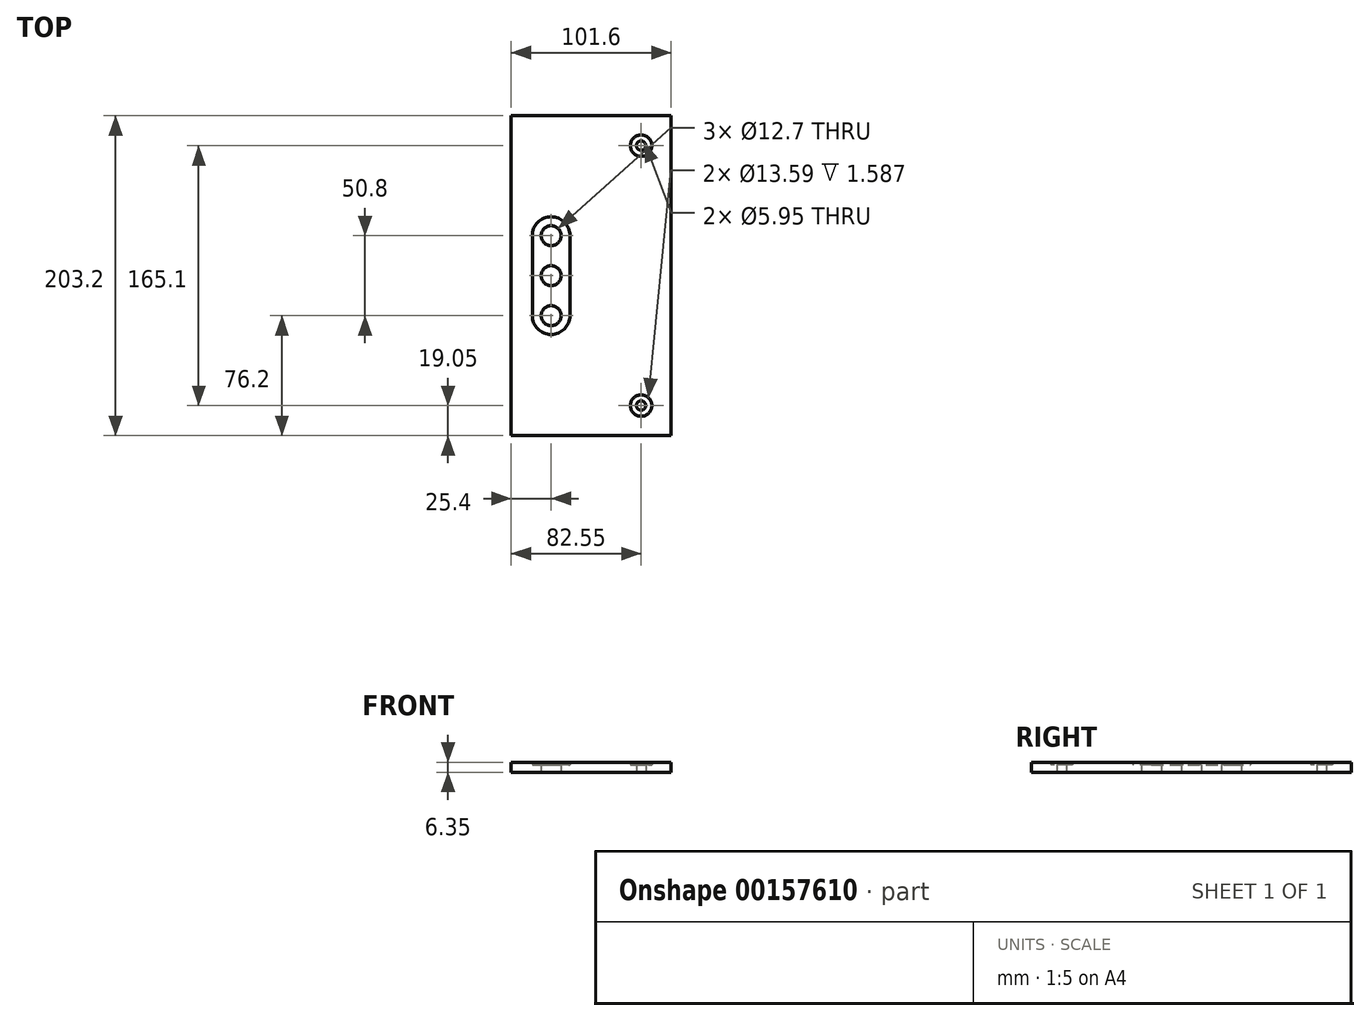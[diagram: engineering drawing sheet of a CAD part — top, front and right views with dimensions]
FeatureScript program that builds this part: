
annotation { "Feature Type Name" : "Feature", "Feature Type Description" : "" }
export const myFeature = defineFeature(function(context is Context, id is Id, definition is map)
    precondition{}
    {
        {
            var Q0;
            Q0=qCreatedBy(makeId("Top.planeOp"),FACE);
            var sketch = newSketch(context, id + "F0", { "sketchPlane" : qUnion([Q0])});
            skLineSegment(sketch, "E0.bottom", {"start": v(0, 0) * mm, "end": v(203.2, 0) * mm});
            skLineSegment(sketch, "E0.top", {"start": v(0, 101.6) * mm, "end": v(203.2, 101.6) * mm});
            skLineSegment(sketch, "E0.left", {"start": v(0, 0) * mm, "end": v(0, 101.6) * mm});
            skLineSegment(sketch, "E0.right", {"start": v(203.2, 0) * mm, "end": v(203.2, 101.6) * mm});
            skCircle(sketch, "E1", {"center": v(76.2, 76.2) * mm, "radius": 6.35 * mm});
            skCircle(sketch, "E2", {"center": v(101.6, 76.2) * mm, "radius": 6.35 * mm});
            skCircle(sketch, "E3", {"center": v(127, 76.2) * mm, "radius": 6.35 * mm});
            skArc(sketch, "E4", {"start": v(76.2, 88.17) * mm, "mid": v(64.23, 76.2) * mm, "end": v(76.2, 64.23) * mm});
            skArc(sketch, "E5", {"start": v(127, 64.23) * mm, "mid": v(138.97, 76.2) * mm, "end": v(127, 88.17) * mm});
            skLineSegment(sketch, "E6", {"start": v(76.2, 88.17) * mm, "end": v(127, 88.17) * mm});
            skLineSegment(sketch, "E7", {"start": v(76.2, 64.23) * mm, "end": v(127, 64.23) * mm});
            skCircle(sketch, "E8", {"center": v(19.05, 19.05) * mm, "radius": 6.8 * mm});
            skCircle(sketch, "E9", {"center": v(19.05, 19.05) * mm, "radius": 2.98 * mm});
            skCircle(sketch, "E10", {"center": v(184.15, 19.05) * mm, "radius": 6.8 * mm});
            skCircle(sketch, "E11", {"center": v(184.15, 19.05) * mm, "radius": 2.98 * mm});
            skSolve(sketch);
        }
        {
            var Q0;
            Q0=makeQuery(id+"F0.imprint","IMPRINT",FACE,{"disambiguationData":[TD([[makeQuery(id+"F0.imprint","IMPRINT",EDGE,{"derivedFrom":sQuery(id+"F0.wireOp",EDGE,"E1")}),-1.0]])]});
            extrude(context, id + "F1", {"entities" : qUnion([Q0]), "depth" : 4.76 * mm});
        }
        {
            var Q0;
            Q0=makeQuery(id+"F0.imprint","IMPRINT",FACE,{"disambiguationData":[TD([[makeQuery(id+"F0.imprint","IMPRINT",EDGE,{"derivedFrom":sQuery(id+"F0.wireOp",EDGE,"E0.bottom")}),1.0]])]});
            extrude(context, id + "F2", {"entities" : qUnion([Q0]), "operationType" : NewBodyOperationType.ADD, "depth" : 6.35 * mm});
        }
        {
            var Q0;
            Q0=makeQuery(id+"F0.imprint","IMPRINT",FACE,{"disambiguationData":[TD([[makeQuery(id+"F0.imprint","IMPRINT",EDGE,{"derivedFrom":sQuery(id+"F0.wireOp",EDGE,"E8")}),1.0]])]});
            extrude(context, id + "F3", {"entities" : qUnion([Q0]), "operationType" : NewBodyOperationType.ADD, "depth" : 4.76 * mm});
        }
        {
            var Q0;
            Q0=makeQuery(id+"F0.imprint","IMPRINT",FACE,{"disambiguationData":[TD([[makeQuery(id+"F0.imprint","IMPRINT",EDGE,{"derivedFrom":sQuery(id+"F0.wireOp",EDGE,"E10")}),1.0]])]});
            extrude(context, id + "F4", {"entities" : qUnion([Q0]), "operationType" : NewBodyOperationType.ADD, "depth" : 4.76 * mm});
        }
        {
            var Q0;
            Q0=makeQuery(id+"F1.opExtrude","SWEPT_BODY",BODY,{"disambiguationData":[OSD([sQuery(id+"F0.wireOp",EDGE,"E1"),sQuery(id+"F0.wireOp",EDGE,"E2"),sQuery(id+"F0.wireOp",EDGE,"E3"),sQuery(id+"F0.wireOp",EDGE,"E4"),sQuery(id+"F0.wireOp",EDGE,"E5"),sQuery(id+"F0.wireOp",EDGE,"E6"),sQuery(id+"F0.wireOp",EDGE,"E7")])]});
            var Q1;
            Q1=makeQuery(id+"F2.opExtrude","SWEPT_EDGE",EDGE,{"disambiguationData":[OSD([sQuery(id+"F0.wireOp",EDGE,"E0.bottom"),sQuery(id+"F0.wireOp",EDGE,"E0.left")])]});
            transform(context, id + "F5", {"entities" : qUnion([Q0]), "transformType" : TransformType.ROTATION, "transformAxis" : qUnion([Q1]), "angle" : 270 * degree, "makeCopy" : false});
        }
        {
            var Q0;
            Q0=makeQuery(id+"F1.opExtrude","SWEPT_BODY",BODY,{"disambiguationData":[OSD([sQuery(id+"F0.wireOp",EDGE,"E1"),sQuery(id+"F0.wireOp",EDGE,"E2"),sQuery(id+"F0.wireOp",EDGE,"E3"),sQuery(id+"F0.wireOp",EDGE,"E4"),sQuery(id+"F0.wireOp",EDGE,"E5"),sQuery(id+"F0.wireOp",EDGE,"E6"),sQuery(id+"F0.wireOp",EDGE,"E7")])]});
            transform(context, id + "F6", {"entities" : qUnion([Q0]), "transformType" : TransformType.TRANSLATION_3D, "dx" : 101.6 * mm, "dy" : 0 * mm, "dz" : 0 * mm, "makeCopy" : false});
        }
    });
